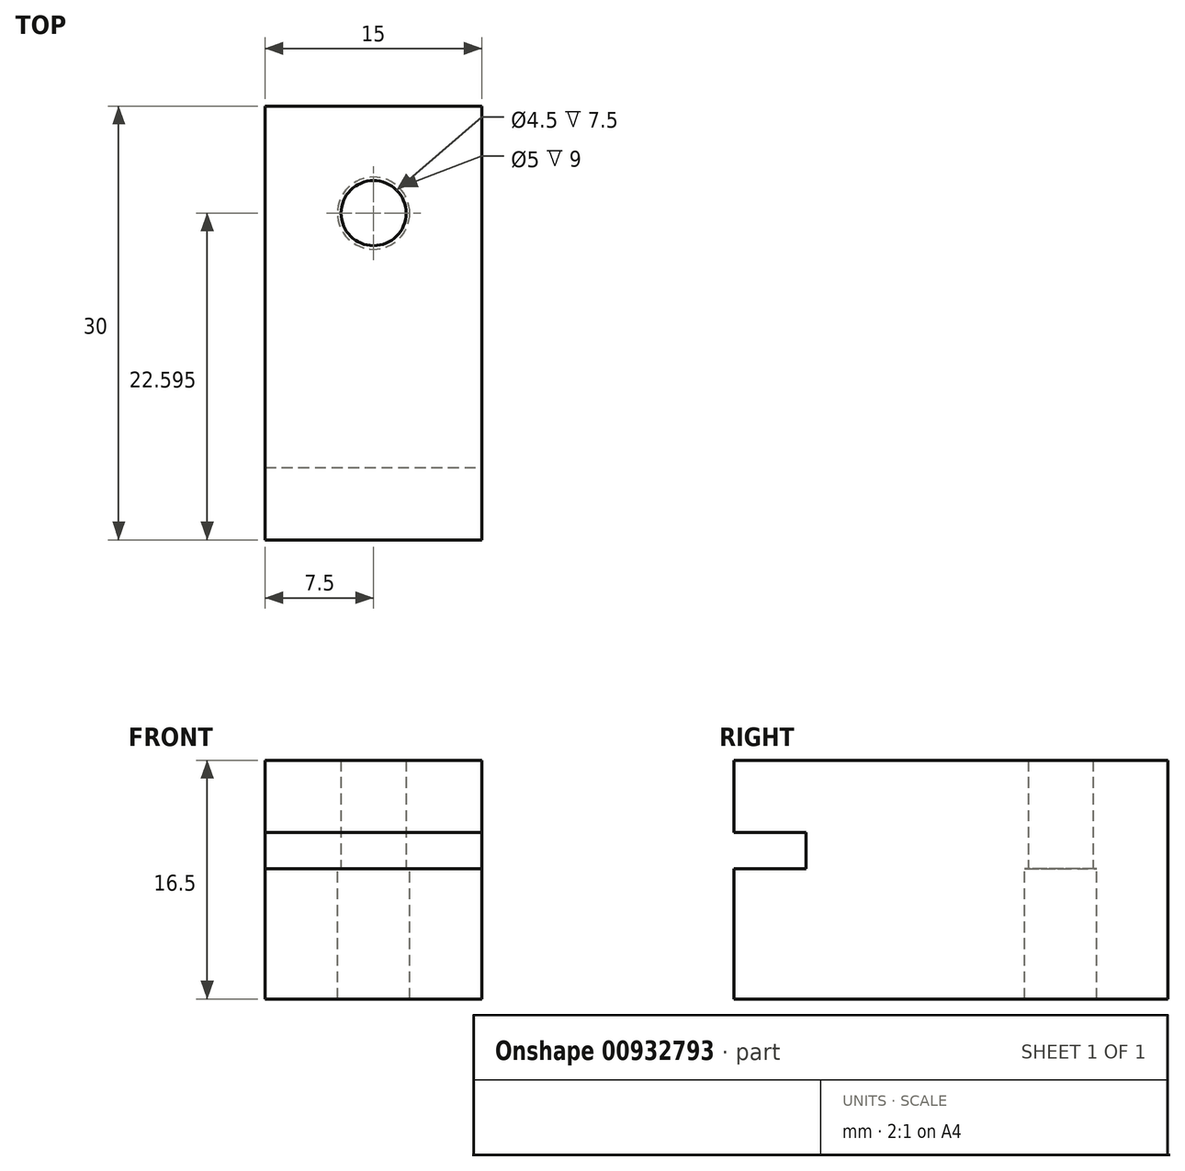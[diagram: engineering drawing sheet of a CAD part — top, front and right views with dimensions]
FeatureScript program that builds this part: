
annotation { "Feature Type Name" : "Feature", "Feature Type Description" : "" }
export const myFeature = defineFeature(function(context is Context, id is Id, definition is map)
    precondition{}
    {
        {
            var Q0;
            Q0=qCreatedBy(makeId("Top.planeOp"),FACE);
            var sketch = newSketch(context, id + "F0", { "sketchPlane" : qUnion([Q0])});
            skLineSegment(sketch, "E0.bottom", {"start": v(0, 0) * mm, "end": v(15, 0) * mm});
            skLineSegment(sketch, "E0.top", {"start": v(0, -25) * mm, "end": v(15, -25) * mm});
            skLineSegment(sketch, "E0.left", {"start": v(0, 0) * mm, "end": v(0, -25) * mm});
            skLineSegment(sketch, "E0.right", {"start": v(15, 0) * mm, "end": v(15, -25) * mm});
            skCircle(sketch, "E1", {"center": v(7.5, -7.4) * mm, "radius": 2.25 * mm});
            skPoint(sketch, "E1.centerSnap0", {"position": v(7.5, -25) * mm});
            skSolve(sketch);
        }
        {
            var Q0;
            Q0 = qSketchRegion(id + "F0", true);
            extrude(context, id + "F1", {"entities" : qUnion([Q0]), "depth" : 2.5 * mm, "offsetDistance" : 25 * mm});
        }
        {
            var Q0;
            Q0=makeQuery(id+"F1.opExtrude","CAP_FACE",FACE,{"disambiguationData":[OSD([sQuery(id+"F0.wireOp",EDGE,"E0.bottom"),sQuery(id+"F0.wireOp",EDGE,"E0.top"),sQuery(id+"F0.wireOp",EDGE,"E0.left"),sQuery(id+"F0.wireOp",EDGE,"E0.right"),sQuery(id+"F0.wireOp",EDGE,"E1")])],"isStart":false});
            var sketch = newSketch(context, id + "F2", { "sketchPlane" : qUnion([Q0])});
            skLineSegment(sketch, "E2.bottom", {"start": v(0, 0) * mm, "end": v(15, 0) * mm});
            skLineSegment(sketch, "E2.top", {"start": v(0, -30) * mm, "end": v(15, -30) * mm});
            skLineSegment(sketch, "E2.left", {"start": v(0, 0) * mm, "end": v(0, -30) * mm});
            skLineSegment(sketch, "E2.right", {"start": v(15, 0) * mm, "end": v(15, -30) * mm});
            skCircle(sketch, "E3", {"center": v(7.5, -7.4) * mm, "radius": 2.25 * mm});
            skSolve(sketch);
        }
        {
            var Q0;
            Q0 = qSketchRegion(id + "F2", true);
            extrude(context, id + "F3", {"entities" : qUnion([Q0]), "operationType" : NewBodyOperationType.ADD, "depth" : 5 * mm, "offsetDistance" : 25 * mm});
        }
        {
            var Q0;
            Q0=makeQuery(id+"F1.opExtrude","CAP_FACE",FACE,{"disambiguationData":[OSD([sQuery(id+"F0.wireOp",EDGE,"E0.bottom"),sQuery(id+"F0.wireOp",EDGE,"E0.top"),sQuery(id+"F0.wireOp",EDGE,"E0.left"),sQuery(id+"F0.wireOp",EDGE,"E0.right"),sQuery(id+"F0.wireOp",EDGE,"E1")])],"isStart":true});
            var sketch = newSketch(context, id + "F4", { "sketchPlane" : qUnion([Q0])});
            skLineSegment(sketch, "E4.bottom", {"start": v(0, 0) * mm, "end": v(15, 0) * mm});
            skLineSegment(sketch, "E4.top", {"start": v(0, 30) * mm, "end": v(15, 30) * mm});
            skLineSegment(sketch, "E4.left", {"start": v(0, 0) * mm, "end": v(0, 30) * mm});
            skLineSegment(sketch, "E4.right", {"start": v(15, 0) * mm, "end": v(15, 30) * mm});
            skCircle(sketch, "E5", {"center": v(7.5, 7.4) * mm, "radius": 2.5 * mm});
            skSolve(sketch);
        }
        {
            var Q0;
            Q0 = qSketchRegion(id + "F4", true);
            extrude(context, id + "F5", {"entities" : qUnion([Q0]), "operationType" : NewBodyOperationType.ADD, "depth" : 9 * mm, "offsetDistance" : 25 * mm});
        }
    });
